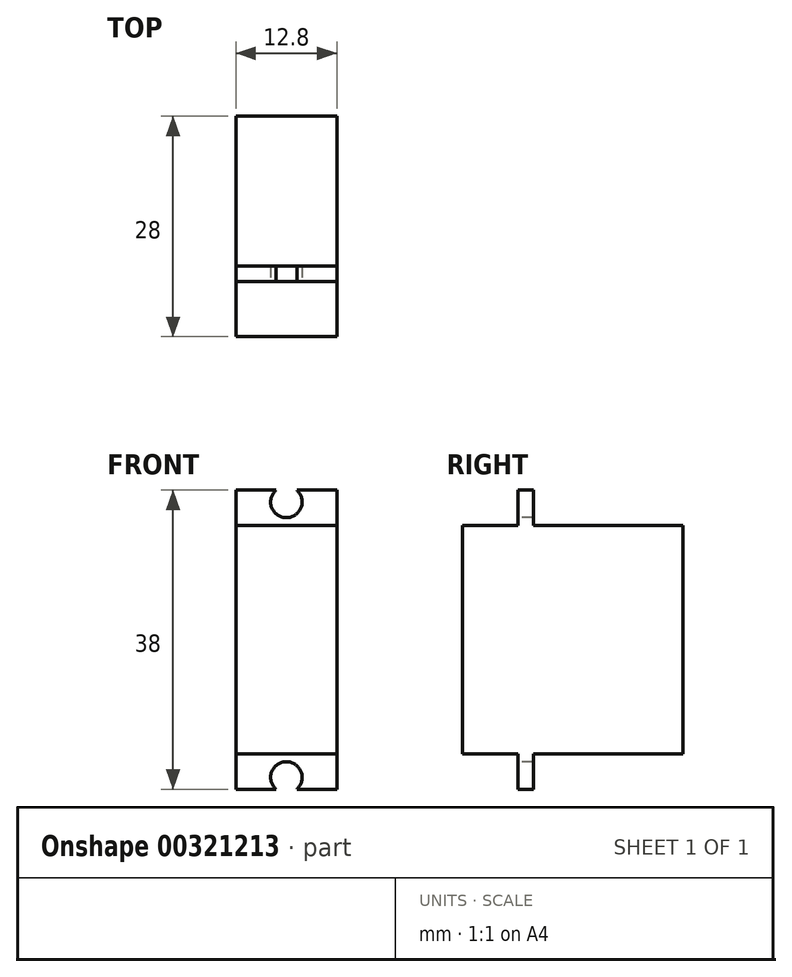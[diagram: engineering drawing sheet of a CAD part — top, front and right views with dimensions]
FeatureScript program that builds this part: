
annotation { "Feature Type Name" : "Feature", "Feature Type Description" : "" }
export const myFeature = defineFeature(function(context is Context, id is Id, definition is map)
    precondition{}
    {
        {
            var Q0;
            Q0=qCreatedBy(makeId("Front.planeOp"),FACE);
            var sketch = newSketch(context, id + "F0", { "sketchPlane" : qUnion([Q0])});
            skLineSegment(sketch, "E0.left", {"start": v(6.4, 14.5) * mm, "end": v(6.4, -14.5) * mm});
            skLineSegment(sketch, "E0.right", {"start": v(-6.4, 14.5) * mm, "end": v(-6.4, -14.5) * mm});
            skPoint(sketch, "E0.middle", {"position": v(0, 0) * mm});
            skLineSegment(sketch, "E1.bottom", {"start": v(6.4, 14.5) * mm, "end": v(-6.4, 14.5) * mm});
            skLineSegment(sketch, "E1.top", {"start": v(6.4, -14.5) * mm, "end": v(-6.4, -14.5) * mm});
            skPoint(sketch, "E0.top.start.orphan", {"position": v(6.4, -19) * mm});
            skPoint(sketch, "E2.orphan", {"position": v(-6.4, -19) * mm});
            skPoint(sketch, "E3.orphan", {"position": v(6.4, 19) * mm});
            skPoint(sketch, "E4.orphan", {"position": v(-6.4, 19) * mm});
            skSolve(sketch);
        }
        {
            var Q0;
            Q0 = qSketchRegion(id + "F0", true);
            extrude(context, id + "F1", {"entities" : qUnion([Q0]), "depth" : 9 * mm, "offsetDistance" : 25 * mm});
        }
        {
            var Q0;
            Q0=makeQuery(id+"F1.opExtrude","CAP_FACE",FACE,{"disambiguationData":[OSD([sQuery(id+"F0.wireOp",EDGE,"E1.bottom"),sQuery(id+"F0.wireOp",EDGE,"E1.top"),sQuery(id+"F0.wireOp",EDGE,"E0.left"),sQuery(id+"F0.wireOp",EDGE,"E0.right")])],"isStart":true});
            var sketch = newSketch(context, id + "F2", { "sketchPlane" : qUnion([Q0])});
            skLineSegment(sketch, "E5.bottom", {"start": v(6.4, 19) * mm, "end": v(-6.4, 19) * mm});
            skLineSegment(sketch, "E5.top", {"start": v(6.4, -19) * mm, "end": v(-6.4, -19) * mm});
            skLineSegment(sketch, "E5.left", {"start": v(6.4, 19) * mm, "end": v(6.4, -19) * mm});
            skLineSegment(sketch, "E5.right", {"start": v(-6.4, 19) * mm, "end": v(-6.4, -19) * mm});
            skPoint(sketch, "E5.middle", {"position": v(0, 0) * mm});
            skSolve(sketch);
        }
        {
            var Q0;
            Q0 = qSketchRegion(id + "F2", true);
            extrude(context, id + "F3", {"entities" : qUnion([Q0]), "operationType" : NewBodyOperationType.ADD, "oppositeDirection" : true, "depth" : 2 * mm, "offsetDistance" : 25 * mm});
        }
        {
            var Q0;
            Q0=makeQuery(id+"F3.boolean.opBoolean","MERGE",FACE,{"derivedFrom":[makeQuery(id+"F1.opExtrude","CAP_FACE",FACE,{"disambiguationData":[OSD([sQuery(id+"F0.wireOp",EDGE,"E1.bottom"),sQuery(id+"F0.wireOp",EDGE,"E1.top"),sQuery(id+"F0.wireOp",EDGE,"E0.left"),sQuery(id+"F0.wireOp",EDGE,"E0.right")])],"isStart":true}),makeQuery(id+"F3.opExtrude","CAP_FACE",FACE,{"disambiguationData":[OSD([sQuery(id+"F2.wireOp",EDGE,"E5.bottom"),sQuery(id+"F2.wireOp",EDGE,"E5.top"),sQuery(id+"F2.wireOp",EDGE,"E5.left"),sQuery(id+"F2.wireOp",EDGE,"E5.right")])],"isStart":true})]});
            var sketch = newSketch(context, id + "F4", { "sketchPlane" : qUnion([Q0])});
            skLineSegment(sketch, "E6.0.0", {"start": v(6.4, -14.5) * mm, "end": v(-6.4, -14.5) * mm});
            skLineSegment(sketch, "E6.0.1", {"start": v(-6.4, -14.5) * mm, "end": v(-6.4, 14.5) * mm});
            skLineSegment(sketch, "E6.0.2", {"start": v(-6.4, 14.5) * mm, "end": v(6.4, 14.5) * mm});
            skLineSegment(sketch, "E6.0.3", {"start": v(6.4, 14.5) * mm, "end": v(6.4, -14.5) * mm});
            skSolve(sketch);
        }
        {
            var Q0;
            Q0 = qSketchRegion(id + "F4", true);
            extrude(context, id + "F5", {"entities" : qUnion([Q0]), "operationType" : NewBodyOperationType.ADD, "depth" : 19 * mm, "offsetDistance" : 25 * mm});
        }
        {
            var Q0;
            {var subQ0=sQuery(id+"F2.wireOp",EDGE,"E5.top");var subQ1=sQuery(id+"F2.wireOp",EDGE,"E5.left");var subQ2=sQuery(id+"F2.wireOp",EDGE,"E5.right");Q0=makeQuery(id+"F3.boolean.opBoolean","SPLIT",FACE,{"disambiguationData":[TD([makeQuery(id+"F1.opExtrude","SWEPT_FACE",FACE,{"disambiguationData":[OSD([sQuery(id+"F0.wireOp",EDGE,"E1.top")])]})])],"derivedFrom":makeQuery(id+"F3.opExtrude","CAP_FACE",FACE,{"disambiguationData":[OSD([sQuery(id+"F2.wireOp",EDGE,"E5.bottom"),subQ0,subQ1,subQ2])],"isStart":false})});}
            var sketch = newSketch(context, id + "F6", { "sketchPlane" : qUnion([Q0])});
            skLineSegment(sketch, "E7", {"start": v(0, -19) * mm, "end": v(0, 18.99) * mm, "construction": true});
            skPoint(sketch, "E8", {"position": v(0, -17.5) * mm});
            skPoint(sketch, "E9", {"position": v(0, 17.5) * mm});
            skLineSegment(sketch, "E10", {"start": v(0, 0) * mm, "end": v(-14.67, 0) * mm, "construction": true});
            skSolve(sketch);
        }
        {
            var Q0;
            Q0=sQuery(id+"F6.wireOp",VERTEX,"E8");
            var Q1;
            Q1=sQuery(id+"F6.wireOp",VERTEX,"E9");
            var Q2;
            Q2=makeQuery(id+"F1.opExtrude","SWEPT_BODY",BODY,{"disambiguationData":[OSD([sQuery(id+"F0.wireOp",EDGE,"E1.bottom"),sQuery(id+"F0.wireOp",EDGE,"E1.top"),sQuery(id+"F0.wireOp",EDGE,"E0.left"),sQuery(id+"F0.wireOp",EDGE,"E0.right")])]});
            hole(context, id + "F7", {"style" : HoleStyle.SIMPLE, "endStyle" : HoleEndStyle.THROUGH, "holeDiameter" : 4 * mm, "majorDiameter" : 5 * mm, "isTappedThrough" : true, "tappedDepth" : 12 * mm, "tapClearance" : 3, "locations" : qUnion([Q0, Q1]), "scope" : qUnion([Q2])});
        }
    });
